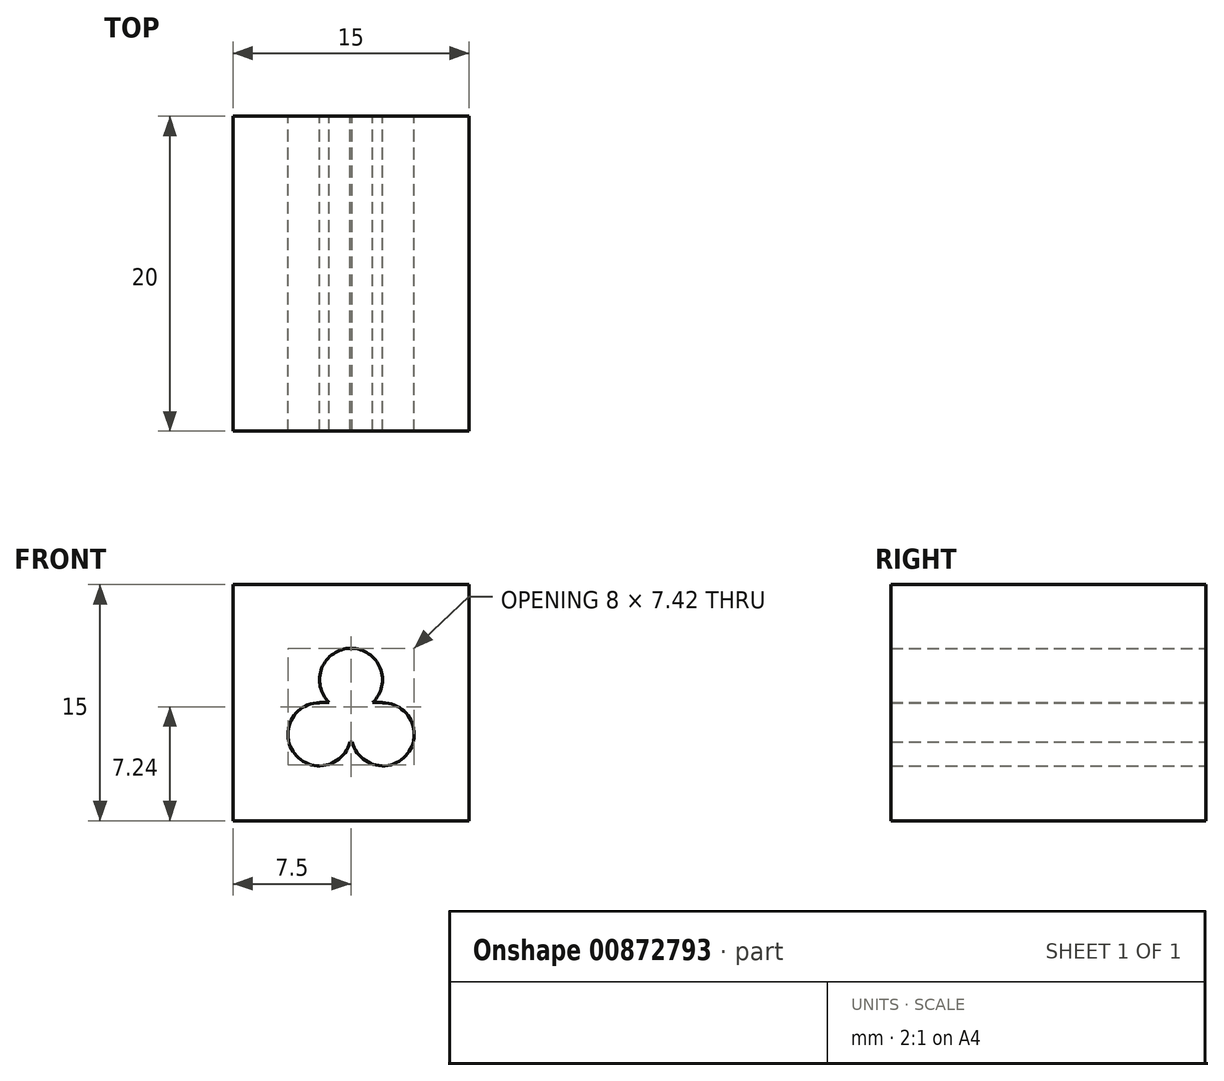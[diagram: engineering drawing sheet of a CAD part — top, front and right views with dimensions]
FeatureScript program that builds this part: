
annotation { "Feature Type Name" : "Feature", "Feature Type Description" : "" }
export const myFeature = defineFeature(function(context is Context, id is Id, definition is map)
    precondition{}
    {
        {
            var Q0;
            Q0=qCreatedBy(makeId("Front.planeOp"),FACE);
            var sketch = newSketch(context, id + "F0", { "sketchPlane" : qUnion([Q0])});
            skLineSegment(sketch, "E0.bottom", {"start": v(7.5, -7.5) * mm, "end": v(-7.5, -7.5) * mm});
            skLineSegment(sketch, "E0.top", {"start": v(7.5, 7.5) * mm, "end": v(-7.5, 7.5) * mm});
            skLineSegment(sketch, "E0.left", {"start": v(7.5, -7.5) * mm, "end": v(7.5, 7.5) * mm});
            skLineSegment(sketch, "E0.right", {"start": v(-7.5, -7.5) * mm, "end": v(-7.5, 7.5) * mm});
            skPoint(sketch, "E0.middle", {"position": v(0, 0) * mm});
            skLineSegment(sketch, "E1", {"start": v(0, 7.5) * mm, "end": v(2, 7.5) * mm});
            skSolve(sketch);
        }
        {
            var Q0;
            Q0 = qSketchRegion(id + "F0", true);
            extrude(context, id + "F1", {"entities" : qUnion([Q0]), "depth" : 20 * mm, "offsetDistance" : 25 * mm});
        }
        {
            var Q0;
            Q0=makeQuery(id+"F1.opExtrude","CAP_FACE",FACE,{"disambiguationData":[OSD([sQuery(id+"F0.wireOp",EDGE,"E0.bottom"),sQuery(id+"F0.wireOp",EDGE,"E0.top"),sQuery(id+"F0.wireOp",EDGE,"E0.left"),sQuery(id+"F0.wireOp",EDGE,"E0.right"),sQuery(id+"F0.wireOp",EDGE,"E1")])],"isStart":true});
            var sketch = newSketch(context, id + "F2", { "sketchPlane" : qUnion([Q0])});
            skLineSegment(sketch, "E2", {"start": v(0, 0) * mm, "end": v(2, 0) * mm});
            skLineSegment(sketch, "E3", {"start": v(2, 0) * mm, "end": v(2, -2) * mm});
            skCircle(sketch, "E4", {"center": v(2, -2) * mm, "radius": 2 * mm});
            skLineSegment(sketch, "E5", {"start": v(0, 0) * mm, "end": v(-2, 0) * mm});
            skLineSegment(sketch, "E6", {"start": v(-2, 0) * mm, "end": v(-2, -2) * mm});
            skCircle(sketch, "E7", {"center": v(-2, -2) * mm, "radius": 2 * mm});
            skCircle(sketch, "E8", {"center": v(0, 1.45) * mm, "radius": 2 * mm});
            skSolve(sketch);
        }
        {
            var Q0;
            Q0 = qSketchRegion(id + "F2", true);
            extrude(context, id + "F3", {"entities" : qUnion([Q0]), "operationType" : NewBodyOperationType.REMOVE, "endBound" : BoundingType.THROUGH_ALL, "oppositeDirection" : true, "depth" : 25 * mm, "offsetDistance" : 25 * mm});
        }
        {
            var Q0;
            Q0=qCreatedBy(makeId("Top.planeOp"),FACE);
            var sketch = newSketch(context, id + "F4", { "sketchPlane" : qUnion([Q0])});
            skLineSegment(sketch, "E9.bottom", {"start": v(-1.2, 2.4) * mm, "end": v(1.3, 2.4) * mm});
            skLineSegment(sketch, "E9.top", {"start": v(-1.2, -20.8) * mm, "end": v(1.3, -20.8) * mm});
            skLineSegment(sketch, "E9.left", {"start": v(-1.2, -20.8) * mm, "end": v(-1.2, 2.4) * mm});
            skLineSegment(sketch, "E9.right", {"start": v(1.3, -20.8) * mm, "end": v(1.3, 2.4) * mm});
            skSolve(sketch);
        }
        {
            var Q0;
            Q0 = qSketchRegion(id + "F4", true);
            extrude(context, id + "F5", {"entities" : qUnion([Q0]), "operationType" : NewBodyOperationType.REMOVE, "oppositeDirection" : true, "depth" : 2.5 * mm, "offsetDistance" : 25 * mm});
        }
    });
